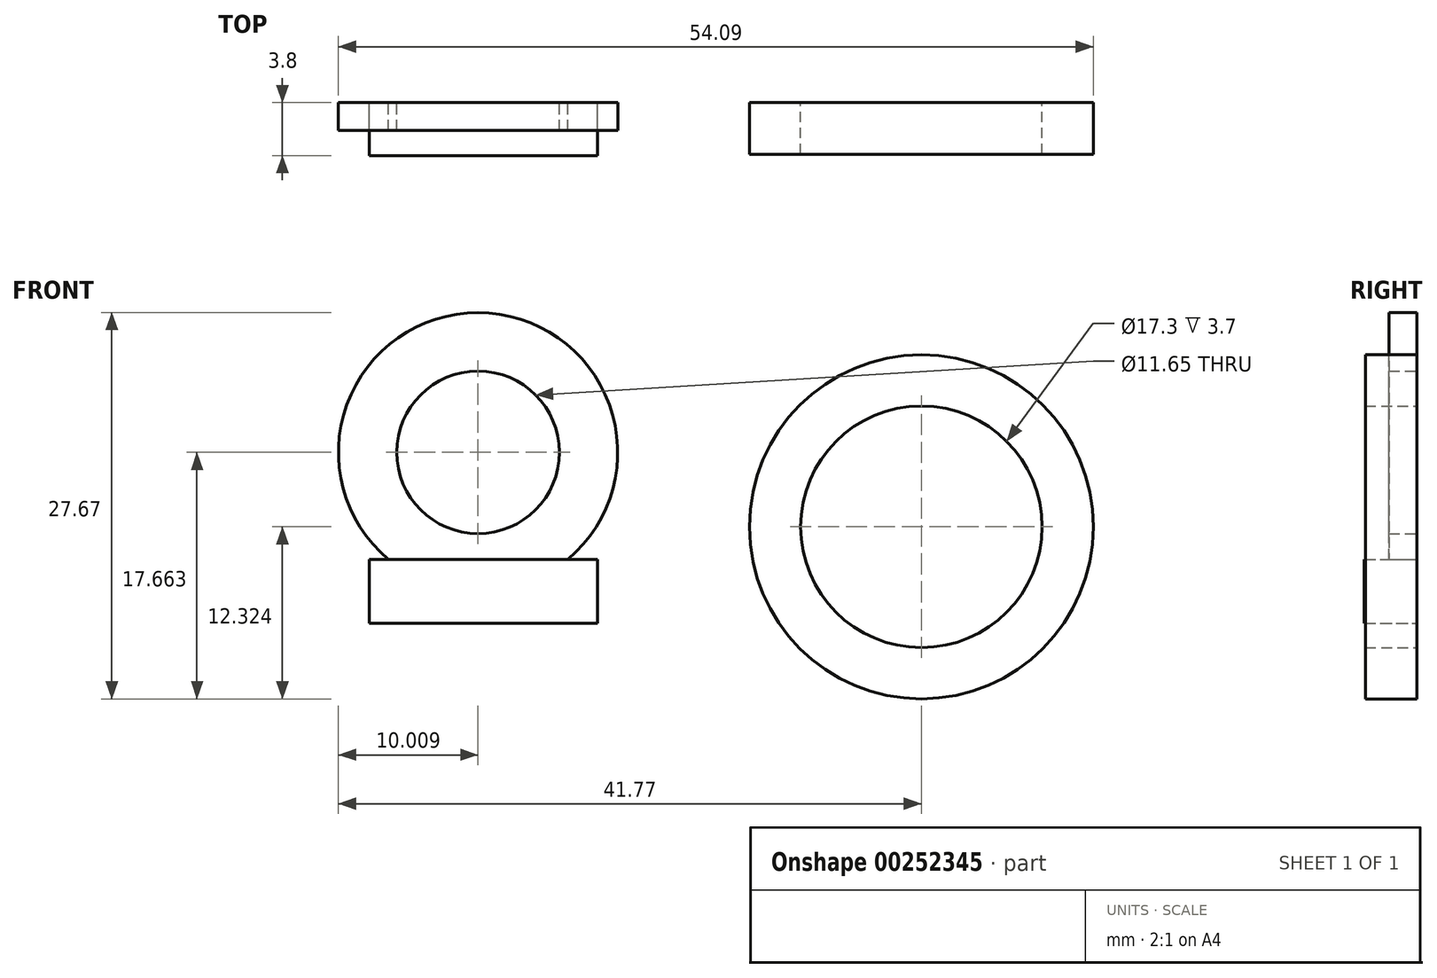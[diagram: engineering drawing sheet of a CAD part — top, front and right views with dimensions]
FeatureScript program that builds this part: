
annotation { "Feature Type Name" : "Feature", "Feature Type Description" : "" }
export const myFeature = defineFeature(function(context is Context, id is Id, definition is map)
    precondition{}
    {
        {
            var Q0;
            Q0=qCreatedBy(makeId("Front.planeOp"),FACE);
            var sketch = newSketch(context, id + "F0", { "sketchPlane" : qUnion([Q0])});
            skCircle(sketch, "E0", {"center": v(-21.46, 33.34) * mm, "radius": 10 * mm});
            skCircle(sketch, "E1", {"center": v(-21.46, 33.34) * mm, "radius": 5.82 * mm});
            skSolve(sketch);
        }
        {
            var Q0;
            Q0=makeQuery(id+"F0.imprint","IMPRINT",FACE,{"disambiguationData":[TD([[makeQuery(id+"F0.imprint","IMPRINT",EDGE,{"derivedFrom":sQuery(id+"F0.wireOp",EDGE,"E0")}),1.0]])]});
            extrude(context, id + "F1", {"entities" : qUnion([Q0]), "depth" : 2 * mm});
        }
        {
            var Q0;
            Q0=qCreatedBy(makeId("Front.planeOp"),FACE);
            var sketch = newSketch(context, id + "F2", { "sketchPlane" : qUnion([Q0])});
            skLineSegment(sketch, "E2.bottom", {"start": v(-29.26, 25.68) * mm, "end": v(-12.9, 25.68) * mm});
            skLineSegment(sketch, "E2.top", {"start": v(-29.26, 21.09) * mm, "end": v(-12.9, 21.09) * mm});
            skLineSegment(sketch, "E2.left", {"start": v(-29.26, 25.68) * mm, "end": v(-29.26, 21.09) * mm});
            skLineSegment(sketch, "E2.right", {"start": v(-12.9, 25.68) * mm, "end": v(-12.9, 21.09) * mm});
            skSolve(sketch);
        }
        {
            var Q0;
            Q0=makeQuery(id+"F2.imprint","IMPRINT",FACE,{"disambiguationData":[TD([[makeQuery(id+"F2.imprint","IMPRINT",EDGE,{"derivedFrom":sQuery(id+"F2.wireOp",EDGE,"E2.bottom")}),-1.0]])]});
            extrude(context, id + "F3", {"entities" : qUnion([Q0]), "operationType" : NewBodyOperationType.ADD, "depth" : 3.8 * mm});
        }
        {
            var Q0;
            Q0=qCreatedBy(makeId("Front.planeOp"),FACE);
            var sketch = newSketch(context, id + "F4", { "sketchPlane" : qUnion([Q0])});
            skCircle(sketch, "E3", {"center": v(10.3, 28) * mm, "radius": 12.32 * mm});
            skCircle(sketch, "E4", {"center": v(10.3, 28) * mm, "radius": 8.65 * mm});
            skSolve(sketch);
        }
        {
            var Q0;
            Q0 = qSketchRegion(id + "F4", true);
            extrude(context, id + "F5", {"entities" : qUnion([Q0]), "depth" : 3.7 * mm});
        }
    });
